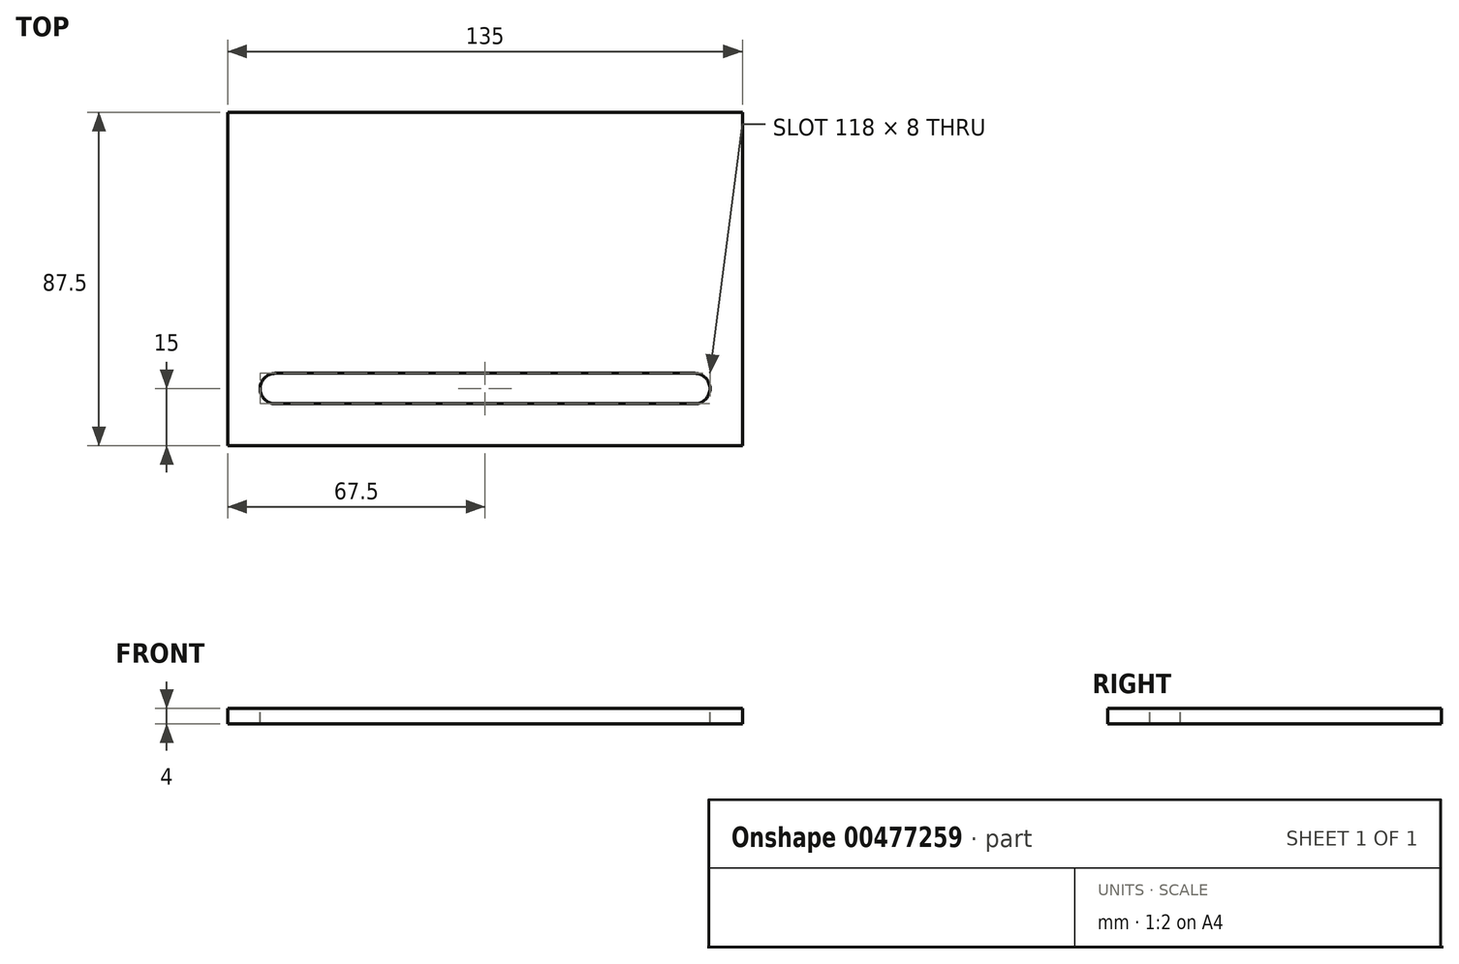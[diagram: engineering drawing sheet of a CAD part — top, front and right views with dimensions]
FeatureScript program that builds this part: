
annotation { "Feature Type Name" : "Feature", "Feature Type Description" : "" }
export const myFeature = defineFeature(function(context is Context, id is Id, definition is map)
    precondition{}
    {
        {
            var Q0;
            Q0=qCreatedBy(makeId("Top.planeOp"),FACE);
            var sketch = newSketch(context, id + "F0", { "sketchPlane" : qUnion([Q0])});
            skLineSegment(sketch, "E0.bottom", {"start": v(67.5, 43.75) * mm, "end": v(-67.5, 43.75) * mm});
            skLineSegment(sketch, "E0.top", {"start": v(67.5, -43.75) * mm, "end": v(-67.5, -43.75) * mm});
            skLineSegment(sketch, "E0.left", {"start": v(67.5, 43.75) * mm, "end": v(67.5, -43.75) * mm});
            skLineSegment(sketch, "E0.right", {"start": v(-67.5, 43.75) * mm, "end": v(-67.5, -43.75) * mm});
            skPoint(sketch, "E0.middle", {"position": v(0, 0) * mm});
            skSolve(sketch);
        }
        {
            var Q0;
            Q0=makeQuery(id+"F0.imprint","IMPRINT",FACE,{"disambiguationData":[TD([[makeQuery(id+"F0.imprint","IMPRINT",EDGE,{"derivedFrom":sQuery(id+"F0.wireOp",EDGE,"E0.bottom")}),1.0]])]});
            extrude(context, id + "F1", {"entities" : qUnion([Q0]), "depth" : 4 * mm});
        }
        {
            var Q0;
            Q0=makeQuery(id+"F1.opExtrude","CAP_FACE",FACE,{"disambiguationData":[OSD([sQuery(id+"F0.wireOp",EDGE,"E0.bottom"),sQuery(id+"F0.wireOp",EDGE,"E0.top"),sQuery(id+"F0.wireOp",EDGE,"E0.left"),sQuery(id+"F0.wireOp",EDGE,"E0.right")])],"isStart":false});
            var sketch = newSketch(context, id + "F2", { "sketchPlane" : qUnion([Q0])});
            skLineSegment(sketch, "E1.bottom", {"start": v(55, -32.75) * mm, "end": v(-55, -32.75) * mm});
            skLineSegment(sketch, "E1.top", {"start": v(55, -24.75) * mm, "end": v(-55, -24.75) * mm});
            skPoint(sketch, "E1.middle", {"position": v(0, -28.75) * mm});
            skArc(sketch, "E2", {"start": v(-55, -24.75) * mm, "mid": v(-59, -28.75) * mm, "end": v(-55, -32.75) * mm});
            skArc(sketch, "E3", {"start": v(55, -32.75) * mm, "mid": v(59, -28.75) * mm, "end": v(55, -24.75) * mm});
            skSolve(sketch);
        }
        {
            var Q0;
            Q0=makeQuery(id+"F2.imprint","IMPRINT",FACE,{"disambiguationData":[TD([[makeQuery(id+"F2.imprint","IMPRINT",EDGE,{"derivedFrom":sQuery(id+"F2.wireOp",EDGE,"E1.bottom")}),-1.0]])]});
            extrude(context, id + "F3", {"entities" : qUnion([Q0]), "operationType" : NewBodyOperationType.REMOVE, "oppositeDirection" : true, "depth" : 25 * mm});
        }
    });
